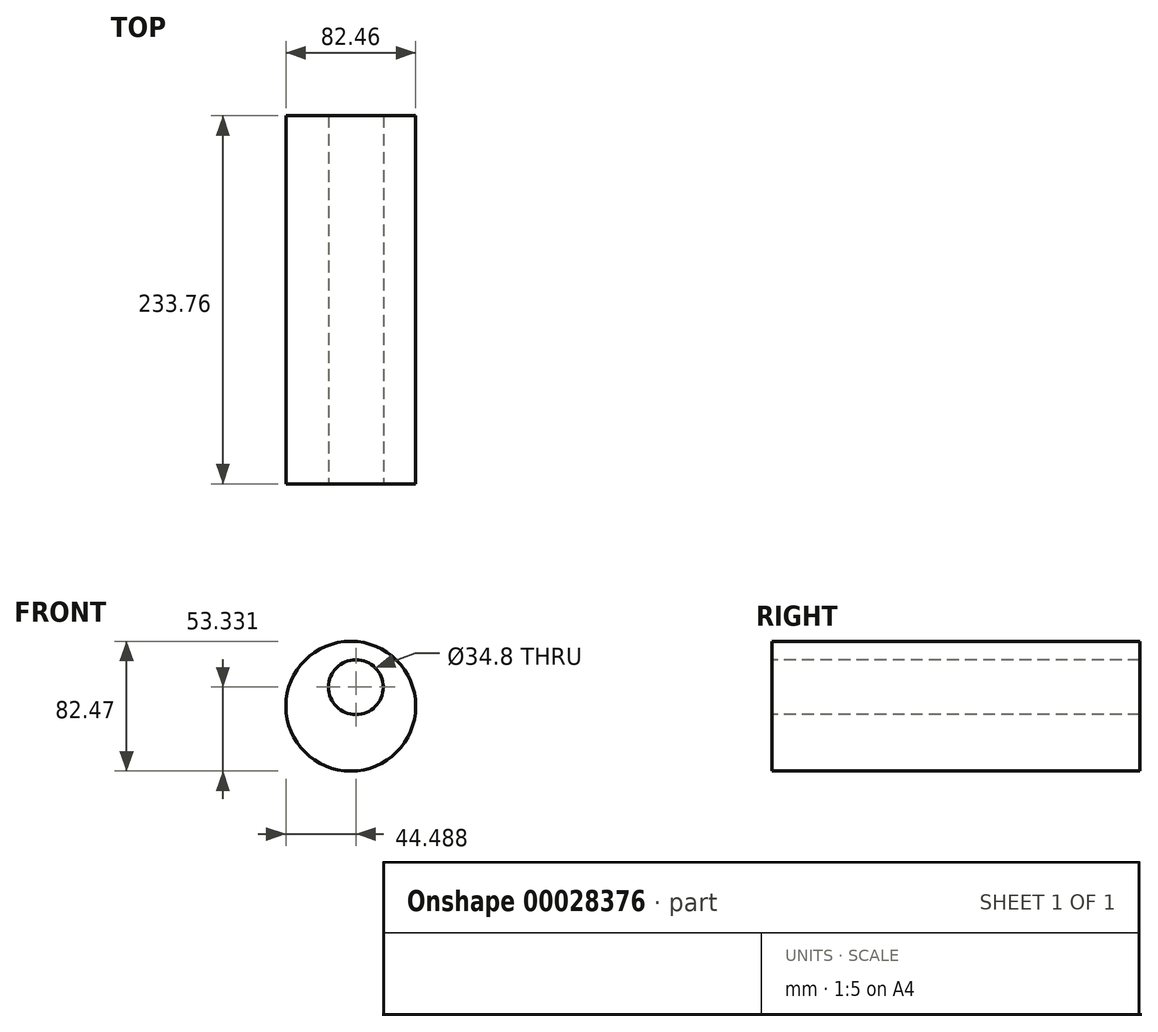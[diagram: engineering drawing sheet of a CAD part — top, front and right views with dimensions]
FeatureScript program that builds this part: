
annotation { "Feature Type Name" : "Feature", "Feature Type Description" : "" }
export const myFeature = defineFeature(function(context is Context, id is Id, definition is map)
    precondition{}
    {
        {
            var Q0;
            Q0=qCreatedBy(makeId("Front.planeOp"),FACE);
            var sketch = newSketch(context, id + "F0", { "sketchPlane" : qUnion([Q0])});
            skCircle(sketch, "E0", {"center": v(-38.34, 20.88) * mm, "radius": 41.23 * mm});
            skSolve(sketch);
        }
        {
            var Q0;
            Q0=makeQuery(id+"F0.imprint","IMPRINT",FACE,{"disambiguationData":[TD([[makeQuery(id+"F0.imprint","IMPRINT",EDGE,{"derivedFrom":sQuery(id+"F0.wireOp",EDGE,"E0")}),1.0]])]});
            extrude(context, id + "F1", {"entities" : qUnion([Q0]), "depth" : 113.57 * mm});
        }
        {
            var Q0;
            Q0=makeQuery(id+"F1.opExtrude","CAP_FACE",FACE,{"disambiguationData":[OSD([sQuery(id+"F0.wireOp",EDGE,"E0")])],"isStart":false});
            var sketch = newSketch(context, id + "F2", { "sketchPlane" : qUnion([Q0])});
            skCircle(sketch, "E1", {"center": v(-35.08, 32.98) * mm, "radius": 17.4 * mm});
            skSolve(sketch);
        }
        {
            var Q0;
            Q0 = qSketchRegion(id + "F2", true);
            extrude(context, id + "F3", {"entities" : qUnion([Q0]), "operationType" : NewBodyOperationType.REMOVE, "oppositeDirection" : true, "depth" : 178.14 * mm});
        }
        {
            var Q0;
            Q0=makeQuery(id+"F1.opExtrude","CAP_FACE",FACE,{"disambiguationData":[OSD([sQuery(id+"F0.wireOp",EDGE,"E0")])],"isStart":false});
            extrude(context, id + "F4", {"entities" : qUnion([Q0]), "operationType" : NewBodyOperationType.ADD, "depth" : 120.2 * mm});
        }
    });
